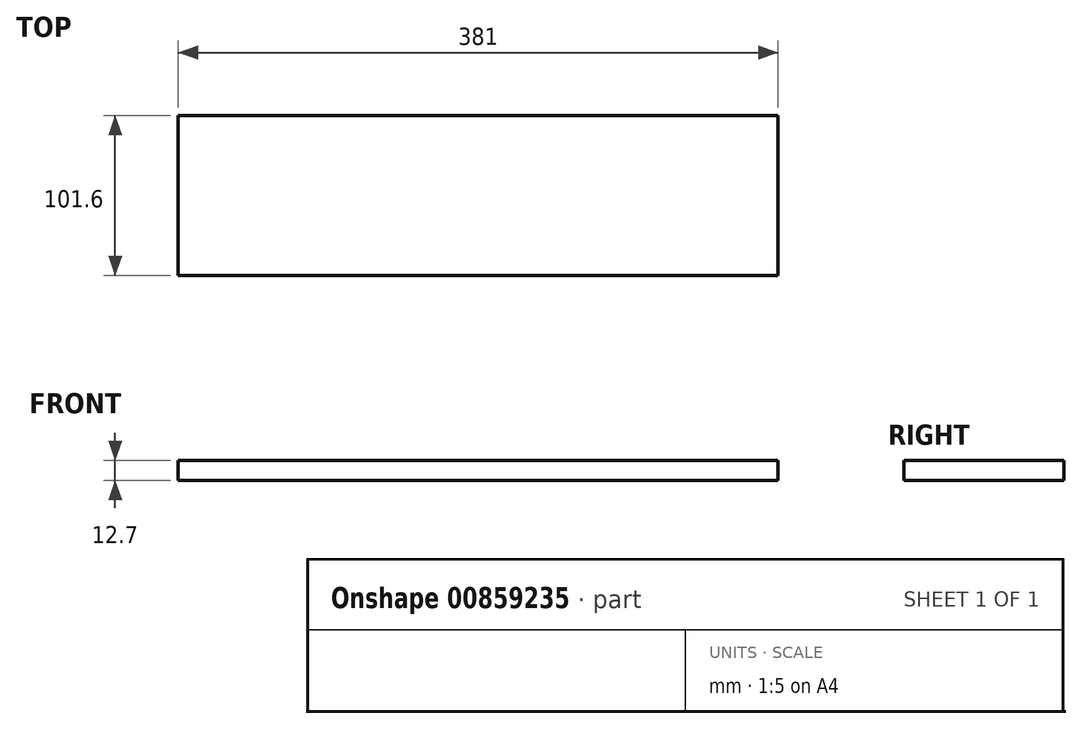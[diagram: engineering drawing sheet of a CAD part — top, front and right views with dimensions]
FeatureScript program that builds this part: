
annotation { "Feature Type Name" : "Feature", "Feature Type Description" : "" }
export const myFeature = defineFeature(function(context is Context, id is Id, definition is map)
    precondition{}
    {
        {
            var Q0;
            Q0=qCreatedBy(makeId("Top.planeOp"),FACE);
            var sketch = newSketch(context, id + "F0", { "sketchPlane" : qUnion([Q0])});
            skLineSegment(sketch, "E0.bottom", {"start": v(0, 0) * mm, "end": v(-381, 0) * mm});
            skLineSegment(sketch, "E0.top", {"start": v(0, 101.6) * mm, "end": v(-381, 101.6) * mm});
            skLineSegment(sketch, "E0.left", {"start": v(0, 0) * mm, "end": v(0, 101.6) * mm});
            skLineSegment(sketch, "E0.right", {"start": v(-381, 0) * mm, "end": v(-381, 101.6) * mm});
            skSolve(sketch);
        }
        {
            var Q0;
            Q0=makeQuery(id+"F0.imprint","IMPRINT",FACE,{"disambiguationData":[TD([[makeQuery(id+"F0.imprint","IMPRINT",EDGE,{"derivedFrom":sQuery(id+"F0.wireOp",EDGE,"E0.bottom")}),-1.0]])]});
            extrude(context, id + "F1", {"entities" : qUnion([Q0]), "depth" : 12.7 * mm, "offsetDistance" : 25.4 * mm});
        }
    });
